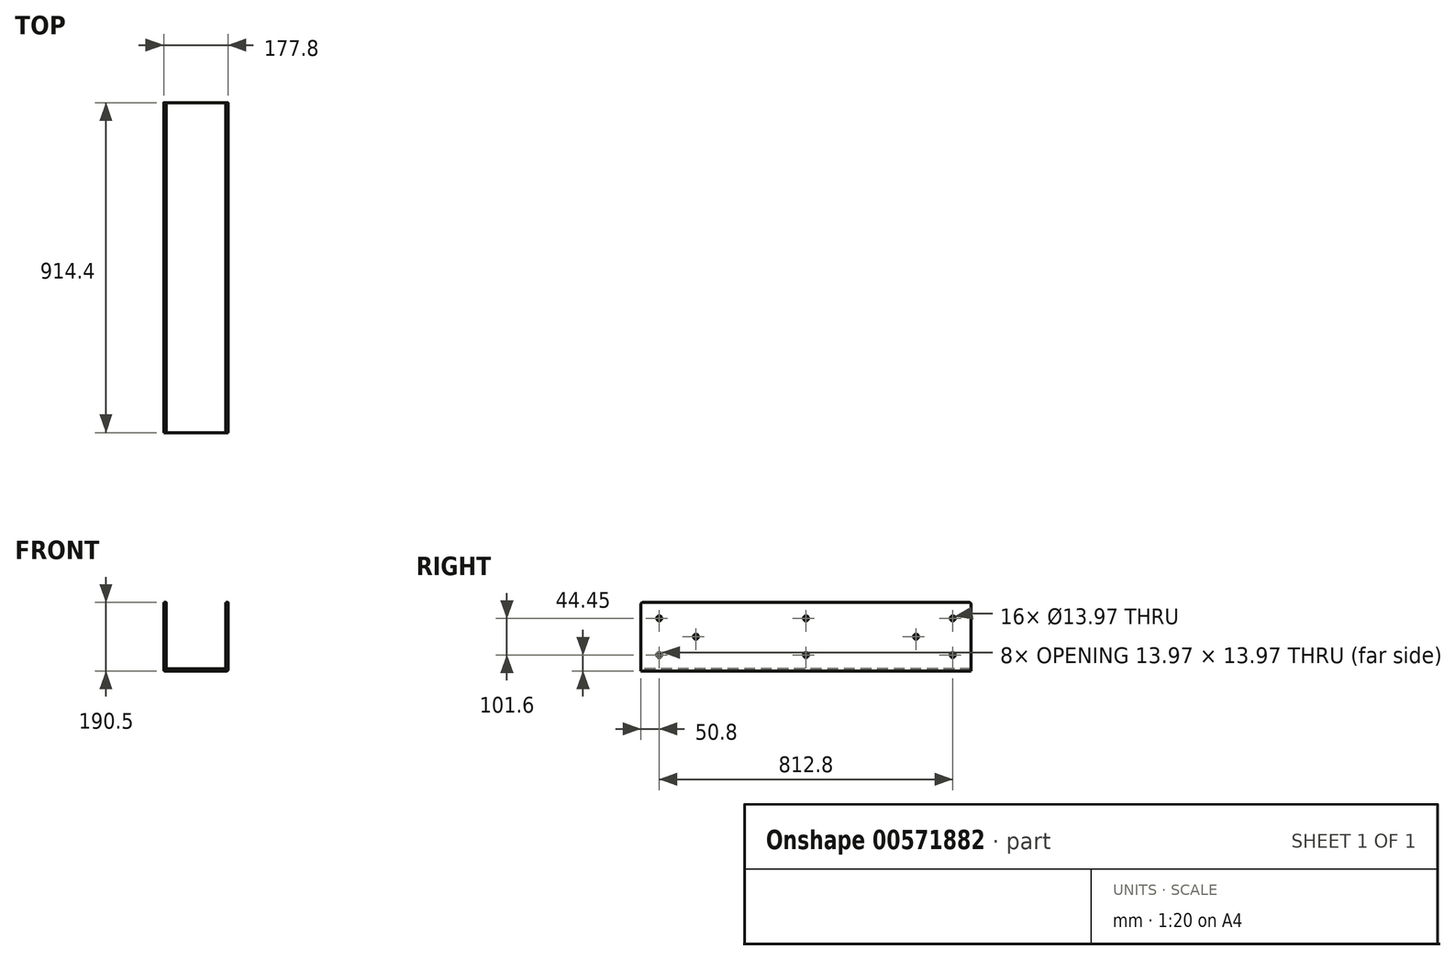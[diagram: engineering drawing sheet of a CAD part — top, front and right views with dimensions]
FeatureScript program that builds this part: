
annotation { "Feature Type Name" : "Feature", "Feature Type Description" : "" }
export const myFeature = defineFeature(function(context is Context, id is Id, definition is map)
    precondition{}
    {
        {
            var Q0;
            Q0=qCreatedBy(makeId("Front.planeOp"),FACE);
            var sketch = newSketch(context, id + "F0", { "sketchPlane" : qUnion([Q0])});
            skLineSegment(sketch, "E0", {"start": v(-82.55, 0) * mm, "end": v(82.55, 0) * mm});
            skLineSegment(sketch, "E1", {"start": v(-82.55, 0) * mm, "end": v(-82.55, 184.15) * mm});
            skLineSegment(sketch, "E2", {"start": v(-82.55, 184.15) * mm, "end": v(-88.9, 184.15) * mm});
            skLineSegment(sketch, "E3", {"start": v(-88.9, 184.15) * mm, "end": v(-88.9, -6.35) * mm});
            skLineSegment(sketch, "E4", {"start": v(-88.9, -6.35) * mm, "end": v(88.9, -6.35) * mm});
            skLineSegment(sketch, "E5", {"start": v(88.9, -6.35) * mm, "end": v(88.9, 184.15) * mm});
            skLineSegment(sketch, "E6", {"start": v(88.9, 184.15) * mm, "end": v(82.55, 184.15) * mm});
            skLineSegment(sketch, "E7", {"start": v(82.55, 184.15) * mm, "end": v(82.55, 0) * mm});
            skSolve(sketch);
        }
        {
            var Q0;
            Q0 = qSketchRegion(id + "F0", true);
            extrude(context, id + "F1", {"entities" : qUnion([Q0]), "oppositeDirection" : true, "depth" : 914.4 * mm, "offsetDistance" : 25.4 * mm});
        }
        {
            var Q0;
            Q0=makeQuery(id+"F1.opExtrude","SWEPT_FACE",FACE,{"disambiguationData":[OSD([sQuery(id+"F0.wireOp",EDGE,"E5")])]});
            var sketch = newSketch(context, id + "F2", { "sketchPlane" : qUnion([Q0])});
            skLineSegment(sketch, "E8.0", {"start": v(914.4, 184.15) * mm, "end": v(0, 184.15) * mm, "construction": true});
            skLineSegment(sketch, "E8.1", {"start": v(0, -6.35) * mm, "end": v(0, 184.15) * mm, "construction": true});
            skLineSegment(sketch, "E8.2", {"start": v(914.4, -6.35) * mm, "end": v(0, -6.35) * mm, "construction": true});
            skLineSegment(sketch, "E8.3", {"start": v(914.4, -6.35) * mm, "end": v(914.4, 184.15) * mm, "construction": true});
            skCircle(sketch, "E9", {"center": v(50.8, 139.7) * mm, "radius": 6.99 * mm});
            skCircle(sketch, "E10", {"center": v(152.4, 88.9) * mm, "radius": 6.99 * mm});
            skCircle(sketch, "E11", {"center": v(457.2, 139.7) * mm, "radius": 6.99 * mm});
            skPoint(sketch, "E11.centerSnap0", {"position": v(457.2, 184.15) * mm});
            skLineSegment(sketch, "E12", {"start": v(457.2, 184.15) * mm, "end": v(457.2, -6.35) * mm, "construction": true});
            skLineSegment(sketch, "E13", {"start": v(0, 88.9) * mm, "end": v(914.4, 88.9) * mm, "construction": true});
            skCircle(sketch, "E14.MirrorC", {"center": v(50.8, 38.1) * mm, "radius": 6.99 * mm});
            skCircle(sketch, "E15.MirrorC", {"center": v(457.2, 38.1) * mm, "radius": 6.99 * mm});
            skCircle(sketch, "E16.MirrorC", {"center": v(762, 88.9) * mm, "radius": 6.99 * mm});
            skCircle(sketch, "E17.MirrorC", {"center": v(863.6, 38.1) * mm, "radius": 6.99 * mm});
            skCircle(sketch, "E18.MirrorC", {"center": v(863.6, 139.7) * mm, "radius": 6.99 * mm});
            skSolve(sketch);
        }
        {
            var Q0;
            Q0 = qSketchRegion(id + "F2", true);
            extrude(context, id + "F3", {"entities" : qUnion([Q0]), "operationType" : NewBodyOperationType.REMOVE, "endBound" : BoundingType.THROUGH_ALL, "oppositeDirection" : true, "depth" : 25.4 * mm, "offsetDistance" : 25.4 * mm});
        }
        {
            var Q0;
            Q0=makeQuery(id+"F1.opExtrude","SWEPT_EDGE",EDGE,{"disambiguationData":[OSD([sQuery(id+"F0.wireOp",EDGE,"E4"),sQuery(id+"F0.wireOp",EDGE,"E5")])]});
            var Q1;
            Q1=makeQuery(id+"F1.opExtrude","SWEPT_EDGE",EDGE,{"disambiguationData":[OSD([sQuery(id+"F0.wireOp",EDGE,"E3"),sQuery(id+"F0.wireOp",EDGE,"E4")])]});
            var Q2;
            Q2=makeQuery(id+"F1.opExtrude","SWEPT_EDGE",EDGE,{"disambiguationData":[OSD([sQuery(id+"F0.wireOp",EDGE,"E0"),sQuery(id+"F0.wireOp",EDGE,"E1")])]});
            var Q3;
            Q3=makeQuery(id+"F1.opExtrude","SWEPT_EDGE",EDGE,{"disambiguationData":[OSD([sQuery(id+"F0.wireOp",EDGE,"E0"),sQuery(id+"F0.wireOp",EDGE,"E7")])]});
            fillet(context, id + "F4", {"entities" : qUnion([Q0, Q1, Q2, Q3]), "radius" : 3.17 * mm, "tangentPropagation" : true, "allowEdgeOverflow" : false});
        }
        {
            var Q0;
            Q0=makeQuery(id+"F1.opExtrude","CAP_EDGE",EDGE,{"disambiguationData":[OSD([sQuery(id+"F0.wireOp",EDGE,"E2")])],"isStart":true});
            var Q1;
            Q1=makeQuery(id+"F1.opExtrude","CAP_EDGE",EDGE,{"disambiguationData":[OSD([sQuery(id+"F0.wireOp",EDGE,"E6")])],"isStart":true});
            var Q2;
            Q2=makeQuery(id+"F1.opExtrude","CAP_EDGE",EDGE,{"disambiguationData":[OSD([sQuery(id+"F0.wireOp",EDGE,"E6")])],"isStart":false});
            var Q3;
            Q3=makeQuery(id+"F1.opExtrude","CAP_EDGE",EDGE,{"disambiguationData":[OSD([sQuery(id+"F0.wireOp",EDGE,"E2")])],"isStart":false});
            fillet(context, id + "F5", {"entities" : qUnion([Q0, Q1, Q2, Q3]), "radius" : 6.35 * mm, "tangentPropagation" : true, "allowEdgeOverflow" : false});
        }
    });
